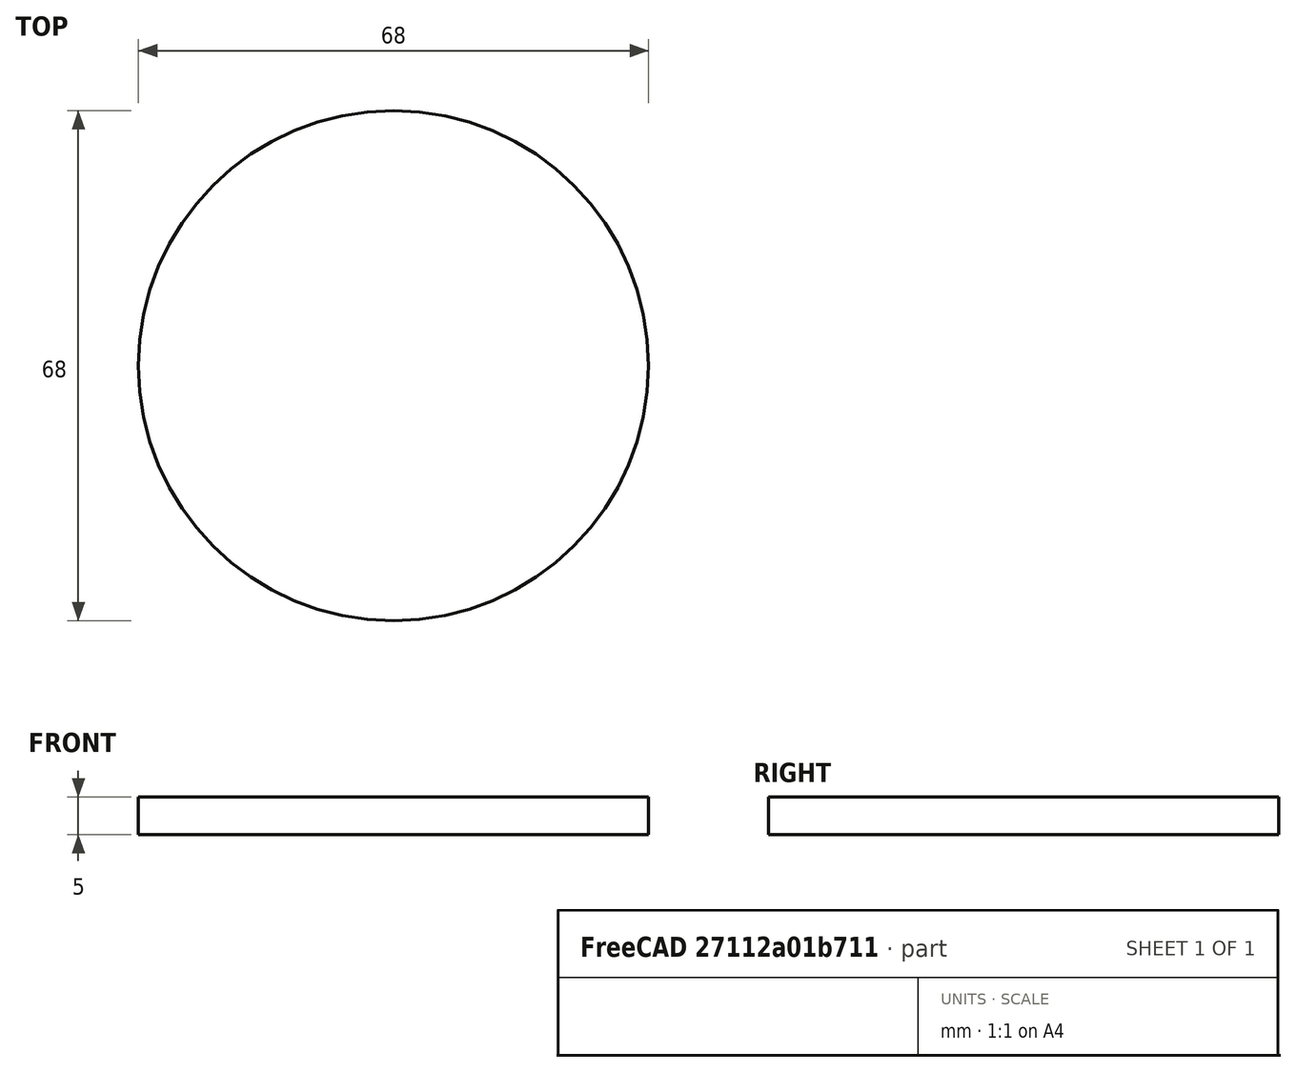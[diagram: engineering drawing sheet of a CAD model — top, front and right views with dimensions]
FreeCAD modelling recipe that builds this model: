
FCSTD DOCUMENT  (FreeCAD 1.0R39109 (Git))
Label: Tail_Hinge_Inner_Pipe_Cover
Comment: Increasing the surface area of the inner tube with a cover helps prevent damage to the outer tube cover caused by friction and wear in larger turbines, especially for Star and larger H shapes.
License: All rights reserved
LicenseURL: http://en.wikipedia.org/wiki/All_rights_reserved
objects: Spreadsheet::Sheet×1, Part::Cylinder×1
note: 1 computed .brp shape members not serialized (recipe doc carries the construction recipe); baked Part::Feature solids carry a one-line shape summary decoded from their .brp
EXTERNAL_REF file=../../../Master_of_Puppets.FCStd obj=Spreadsheet
EXTERNAL_REF file=../../../Master_of_Puppets.FCStd obj=Tail

FEATURE [Spreadsheet::Sheet] Spreadsheet
  cells = A1='Inputs; A2='PipeThickness; B2(PipeThickness)==Master_of_Puppets#Spreadsheet.PipeThickness; A3='HingeInnerPipeCoverThickness; B3(HingeInnerPipeCoverThickness)==Master_of_Puppets#Tail.HingeInnerPipeCoverThickness; A4='HingeInnerPipeRadius; B4(HingeInnerPipeRadius)==Master_of_Puppets#Tail.HingeInnerPipeRadius; A5='Calculated; A6='HingeInnerPipeCoverRadius; B6(HingeInnerPipeCoverRadius)==HingeInnerPipeRadius - PipeThickness / 2
FEATURE [Part::Cylinder] Cylinder  label="Tail_Hinge_Inner_Pipe_Cover"
  Angle = 360
  AttacherType = Attacher::AttachEngine3D
  FirstAngle = 0
  Height = 5
  Openafpm_Flat = true
  Radius = 34
  SecondAngle = 0
  expr: Height = Spreadsheet.HingeInnerPipeCoverThickness
  expr: Radius = Spreadsheet.HingeInnerPipeCoverRadius
